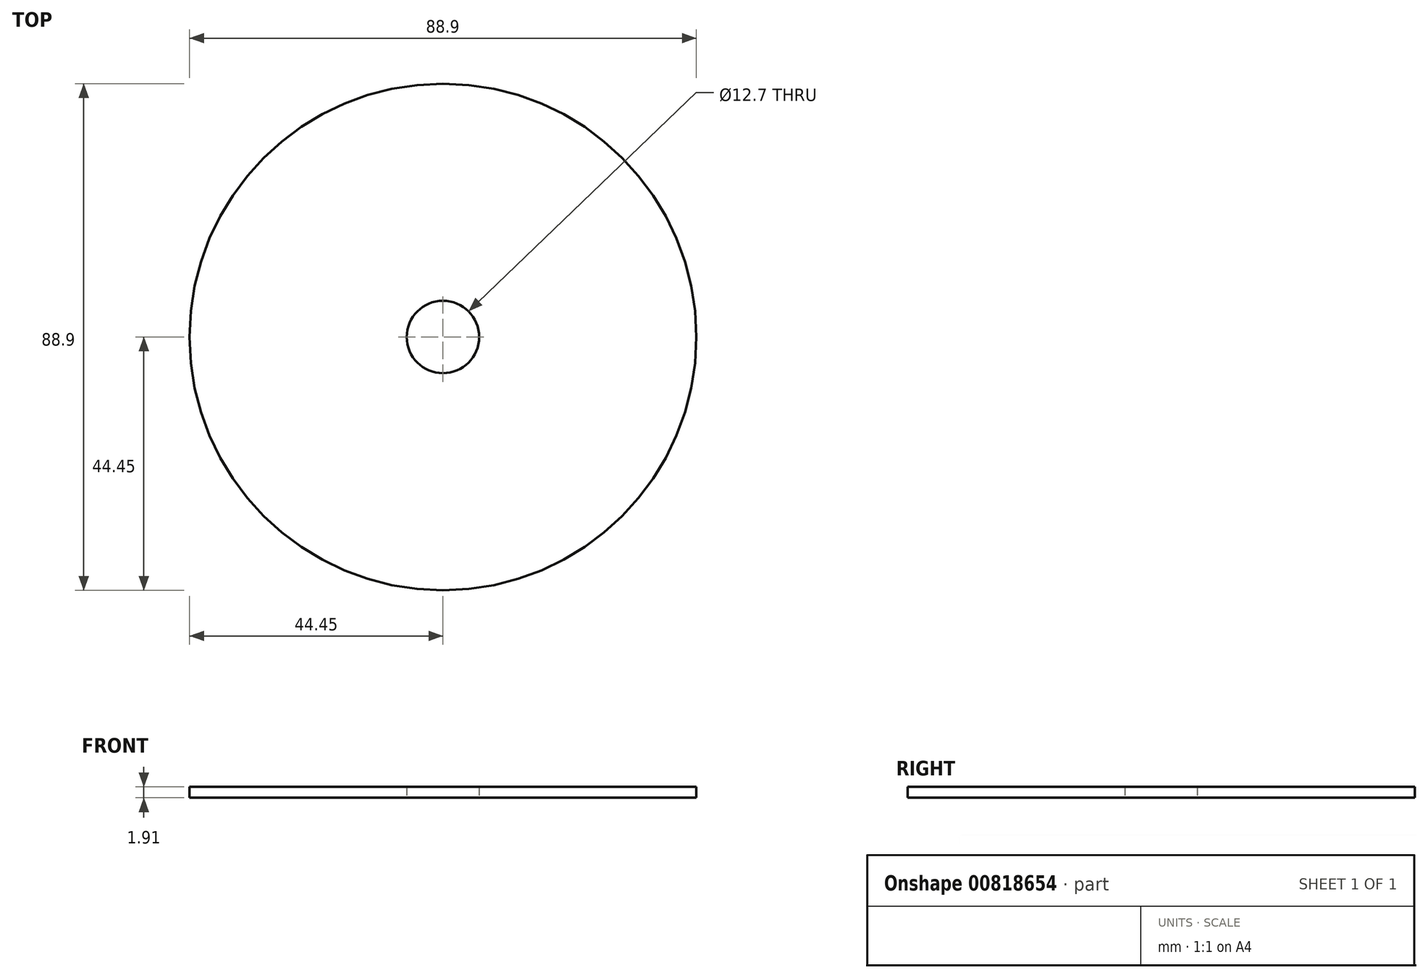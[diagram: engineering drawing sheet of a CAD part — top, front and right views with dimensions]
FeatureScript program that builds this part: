
annotation { "Feature Type Name" : "Feature", "Feature Type Description" : "" }
export const myFeature = defineFeature(function(context is Context, id is Id, definition is map)
    precondition{}
    {
        {
            var Q0;
            Q0=qCreatedBy(makeId("Top.planeOp"),FACE);
            var sketch = newSketch(context, id + "F0", { "sketchPlane" : qUnion([Q0])});
            skCircle(sketch, "E0", {"center": v(0, 0) * mm, "radius": 44.45 * mm});
            skCircle(sketch, "E1", {"center": v(0, 0) * mm, "radius": 6.35 * mm});
            skSolve(sketch);
        }
        {
            var Q0;
            Q0=makeQuery(id+"F0.imprint","IMPRINT",FACE,{"disambiguationData":[TD([[makeQuery(id+"F0.imprint","IMPRINT",EDGE,{"derivedFrom":sQuery(id+"F0.wireOp",EDGE,"E0")}),1.0]])]});
            extrude(context, id + "F1", {"entities" : qUnion([Q0]), "depth" : 1.9 * mm, "offsetDistance" : 25.4 * mm});
        }
    });
